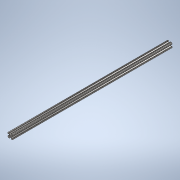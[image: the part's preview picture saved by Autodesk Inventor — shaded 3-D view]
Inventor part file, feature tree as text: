
AUTODESK INVENTOR PART (.ipt)
format: ipt  version: 2020 (Build 240168000, 168)  size: 244,736 bytes
history: native  units: in
note: dims shown in document units (in); Inventor stores cm internally (conversion verified against a paired STEP export)
features: extrude x1, sketch x1
ambient origin geometry x8: Origin, YZ Plane, XZ Plane, XY Plane, X Axis, Y Axis, Z Axis, Center Point
bodies: Solid1 (feature_tree)
feature tree (2):
  extrude  "Extrusion1"  [1 undecoded]
  sketch  "Sketch1"  dims[d0=33.0in d1=0.0in]
note: 1 required parameter value undecoded (feature->parameter linkage not recoverable at this tier; creation-order binding heuristic only, values carry confidence <= 0.55)
